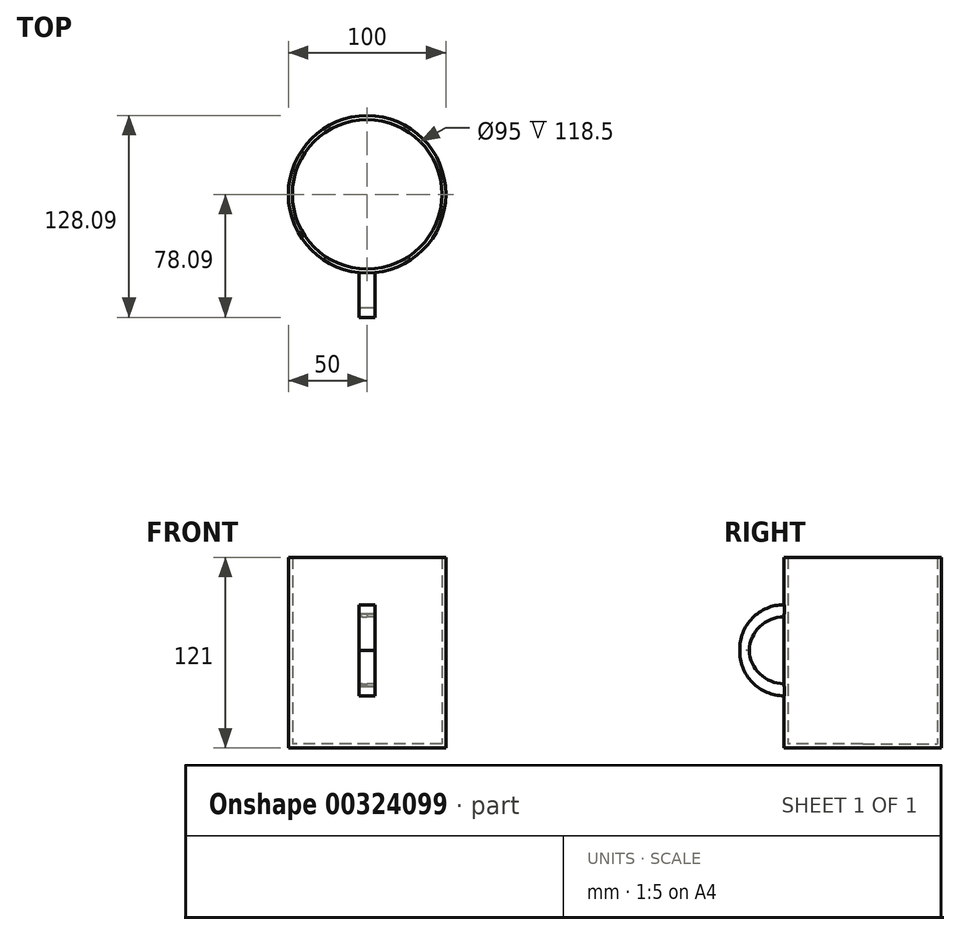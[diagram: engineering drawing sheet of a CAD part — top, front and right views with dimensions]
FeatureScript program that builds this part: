
annotation { "Feature Type Name" : "Feature", "Feature Type Description" : "" }
export const myFeature = defineFeature(function(context is Context, id is Id, definition is map)
    precondition{}
    {
        {
            var Q0;
            Q0=qCreatedBy(makeId("Top.planeOp"),FACE);
            var sketch = newSketch(context, id + "F0", { "sketchPlane" : qUnion([Q0])});
            skCircle(sketch, "E0", {"center": v(0, 0) * mm, "radius": 50 * mm});
            skSolve(sketch);
        }
        {
            var Q0;
            Q0 = qSketchRegion(id + "F0", true);
            extrude(context, id + "F1", {"entities" : qUnion([Q0]), "depth" : 120 * mm});
        }
        {
            var Q0;
            Q0=makeQuery(id+"F1.opExtrude","CAP_FACE",FACE,{"disambiguationData":[OSD([sQuery(id+"F0.wireOp",EDGE,"E0")])],"isStart":false});
            shell(context, id + "F2", {"entities" : qUnion([Q0]), "thickness" : 2.5 * mm});
        }
        {
            var Q0;
            Q0=qCreatedBy(makeId("Right.planeOp"),FACE);
            var sketch = newSketch(context, id + "F3", { "sketchPlane" : qUnion([Q0])});
            skPoint(sketch, "E1", {"position": v(-50, 0) * mm});
            skPoint(sketch, "E2", {"position": v(-50, 33.06) * mm});
            skPoint(sketch, "E3", {"position": v(-50, 89.25) * mm});
            skArc(sketch, "E4", {"start": v(-50, 89.25) * mm, "mid": v(-78.1, 61.16) * mm, "end": v(-50, 33.06) * mm});
            skArc(sketch, "E5.0", {"start": v(-50, 83.25) * mm, "mid": v(-72.1, 61.16) * mm, "end": v(-50, 39.06) * mm});
            skLineSegment(sketch, "E6", {"start": v(-50, 89.25) * mm, "end": v(-50, 83.25) * mm});
            skLineSegment(sketch, "E7", {"start": v(-50, 33.06) * mm, "end": v(-50, 39.06) * mm});
            skSolve(sketch);
        }
        {
            var Q0;
            Q0 = qSketchRegion(id + "F3", true);
            extrude(context, id + "F4", {"entities" : qUnion([Q0]), "operationType" : NewBodyOperationType.ADD, "depth" : 5 * mm});
        }
        {
            var Q0;
            Q0=makeQuery(id+"F1.opExtrude","SWEPT_BODY",BODY,{"disambiguationData":[OSD([sQuery(id+"F0.wireOp",EDGE,"E0")])]});
            var Q1;
            Q1=qCreatedBy(makeId("Right.planeOp"),FACE);
            mirror(context, id + "F5", {"operationType" : NewBodyOperationType.ADD, "entities" : qUnion([Q0]), "mirrorPlane" : qUnion([Q1])});
        }
        {
            var Q0;
            Q0=makeQuery(id+"F5.opPattern","COPY",FACE,{"derivedFrom":makeQuery(id+"F4.opExtrude","SWEPT_FACE",FACE,{"disambiguationData":[OSD([sQuery(id+"F3.wireOp",EDGE,"E7")])]}),"instanceName":"1"});
            extrude(context, id + "F6", {"entities" : qUnion([Q0]), "operationType" : NewBodyOperationType.ADD, "depth" : 0.5 * mm});
        }
        {
            var Q0;
            Q0=makeQuery(id+"F1.opExtrude","SWEPT_BODY",BODY,{"disambiguationData":[OSD([sQuery(id+"F0.wireOp",EDGE,"E0")])]});
            var Q1;
            Q1=qCreatedBy(makeId("Right.planeOp"),FACE);
            mirror(context, id + "F7", {"operationType" : NewBodyOperationType.ADD, "entities" : qUnion([Q0]), "mirrorPlane" : qUnion([Q1])});
        }
        {
            var Q0;
            Q0=qCreatedBy(makeId("Top.planeOp"),FACE);
            cPlane(context, id + "F8", {"entities" : qUnion([Q0]), "cplaneType" : CPlaneType.OFFSET, "offset" : 62 * mm, "width" : 150 * mm, "height" : 150 * mm});
        }
        {
            var Q0;
            Q0=makeQuery(id+"F1.opExtrude","SWEPT_BODY",BODY,{"disambiguationData":[OSD([sQuery(id+"F0.wireOp",EDGE,"E0")])]});
            var Q1;
            Q1=qCreatedBy(id+"F8.planeOp",FACE);
            mirror(context, id + "F9", {"operationType" : NewBodyOperationType.ADD, "entities" : qUnion([Q0]), "mirrorPlane" : qUnion([Q1])});
        }
        {
            var Q0;
            Q0=makeQuery(id+"F9.opPattern","COPY",FACE,{"derivedFrom":makeQuery(id+"F1.opExtrude","CAP_FACE",FACE,{"disambiguationData":[OSD([sQuery(id+"F0.wireOp",EDGE,"E0")])],"isStart":true}),"instanceName":"1"});
            extrude(context, id + "F10", {"entities" : qUnion([Q0]), "operationType" : NewBodyOperationType.REMOVE, "oppositeDirection" : true, "depth" : 2 * mm});
        }
        {
            var Q0;
            Q0=makeQuery(id+"F10.boolean.opBoolean","COPY",FACE,{"derivedFrom":makeQuery(id+"F10.opExtrude","CAP_FACE",FACE,{"disambiguationData":[OSD([sQuery(id+"F0.wireOp",EDGE,"E0")])],"isStart":false})});
            extrude(context, id + "F11", {"entities" : qUnion([Q0]), "operationType" : NewBodyOperationType.REMOVE, "oppositeDirection" : true, "depth" : 1 * mm});
        }
        {
            var Q0;
            Q0=makeQuery(id+"F5.opPattern","COPY",EDGE,{"derivedFrom":makeQuery(id+"F4.opExtrude","CAP_EDGE",EDGE,{"disambiguationData":[OSD([sQuery(id+"F3.wireOp",EDGE,"E5.0")])],"isStart":false}),"instanceName":"1"});
            var Q1;
            {var subQ0=sQuery(id+"F3.wireOp",EDGE,"E7");var subQ1=sQuery(id+"F3.wireOp",EDGE,"E4");Q1=makeQuery(id+"F9.opPattern","COPY",EDGE,{"derivedFrom":makeQuery(id+"F6.boolean.opBoolean","MERGE",EDGE,{"derivedFrom":[makeQuery(id+"F5.opPattern","COPY",EDGE,{"derivedFrom":makeQuery(id+"F4.opExtrude","SWEPT_EDGE",EDGE,{"disambiguationData":[OSD([subQ1,subQ0])]}),"instanceName":"1"}),makeQuery(id+"F6.opExtrude","CAP_EDGE",EDGE,{"disambiguationData":[OSD([subQ1,subQ0])],"isStart":true})]}),"instanceName":"1"});}
            var Q2;
            {var subQ0=sQuery(id+"F3.wireOp",EDGE,"E7");var subQ1=sQuery(id+"F3.wireOp",EDGE,"E4");var subQ2=makeQuery(id+"F4.opExtrude","SWEPT_EDGE",EDGE,{"disambiguationData":[OSD([subQ1,subQ0])]});Q2=makeQuery(id+"F9.opPattern","COPY",EDGE,{"derivedFrom":makeQuery(id+"F7.boolean.opBoolean","MERGE",EDGE,{"derivedFrom":[subQ2,makeQuery(id+"F7.opPattern","COPY",EDGE,{"derivedFrom":makeQuery(id+"F6.boolean.opBoolean","MERGE",EDGE,{"derivedFrom":[makeQuery(id+"F5.opPattern","COPY",EDGE,{"derivedFrom":subQ2,"instanceName":"1"}),makeQuery(id+"F6.opExtrude","CAP_EDGE",EDGE,{"disambiguationData":[OSD([subQ1,subQ0])],"isStart":true})]}),"instanceName":"1"})]}),"instanceName":"1"});}
            var Q3;
            Q3=makeQuery(id+"F9.opPattern","COPY",EDGE,{"derivedFrom":makeQuery(id+"F7.opPattern","COPY",EDGE,{"derivedFrom":makeQuery(id+"F6.boolean.opBoolean","INTERSECT",EDGE,{"derivedFrom":[makeQuery(id+"F1.opExtrude","SWEPT_FACE",FACE,{"disambiguationData":[OSD([sQuery(id+"F0.wireOp",EDGE,"E0")])]}),makeQuery(id+"F6.opExtrude","SWEPT_FACE",FACE,{"disambiguationData":[OSD([sQuery(id+"F3.wireOp",EDGE,"E7")])]})]}),"instanceName":"1"}),"instanceName":"1"});
            fillet(context, id + "F12", {"entities" : qUnion([Q0, Q1, Q2, Q3]), "radius" : 2 * mm, "tangentPropagation" : true, "allowEdgeOverflow" : false});
        }
    });
